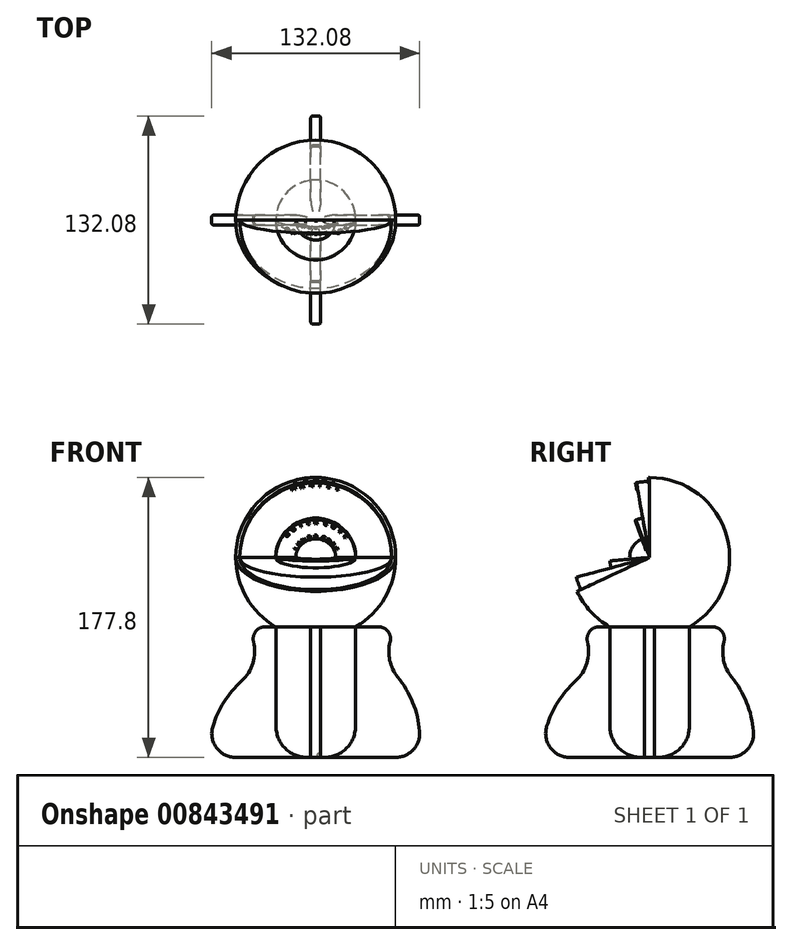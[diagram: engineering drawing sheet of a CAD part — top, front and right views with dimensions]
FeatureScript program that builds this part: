
annotation { "Feature Type Name" : "Feature", "Feature Type Description" : "" }
export const myFeature = defineFeature(function(context is Context, id is Id, definition is map)
    precondition{}
    {
        {
            var Q0;
            Q0=qCreatedBy(makeId("Front.planeOp"),FACE);
            var sketch = newSketch(context, id + "F0", { "sketchPlane" : qUnion([Q0])});
            skCircle(sketch, "E0", {"center": v(0, 0) * mm, "radius": 50.8 * mm});
            skLineSegment(sketch, "E1", {"start": v(-50.8, 0) * mm, "end": v(50.8, 0) * mm});
            skSolve(sketch);
        }
        {
            var Q0;
            {var subQ0=sQuery(id+"F0.wireOp",EDGE,"E1");Q0=makeQuery(id+"F0.imprint","IMPRINT",FACE,{"disambiguationData":[TD([[makeQuery(id+"F0.imprint","IMPRINT",EDGE,{"derivedFrom":subQ0}),1.0]])]});}
            var Q1;
            Q1=sQuery(id+"F0.wireOp",EDGE,"E1");
            revolve(context, id + "F1", {"surfaceOperationType" : NewSurfaceOperationType.NEW, "entities" : qUnion([Q0]), "axis" : qUnion([Q1]), "revolveType" : RevolveType.TWO_DIRECTIONS, "angle" : 0 * degree, "angleBack" : 115 * degree});
        }
        {
            var Q0;
            Q0=qCreatedBy(makeId("Front.planeOp"),FACE);
            var sketch = newSketch(context, id + "F2", { "sketchPlane" : qUnion([Q0])});
            skCircle(sketch, "E2", {"center": v(0, 0) * mm, "radius": 12.7 * mm});
            skLineSegment(sketch, "E3", {"start": v(-12.7, 0) * mm, "end": v(12.7, 0) * mm});
            skSolve(sketch);
        }
        {
            var Q0;
            {var subQ0=sQuery(id+"F2.wireOp",EDGE,"E3");Q0=makeQuery(id+"F2.imprint","IMPRINT",FACE,{"disambiguationData":[TD([[makeQuery(id+"F2.imprint","IMPRINT",EDGE,{"derivedFrom":subQ0}),1.0]])]});}
            var Q1;
            Q1=sQuery(id+"F2.wireOp",EDGE,"E3");
            revolve(context, id + "F3", {"operationType" : NewBodyOperationType.ADD, "surfaceOperationType" : NewSurfaceOperationType.NEW, "entities" : qUnion([Q0]), "axis" : qUnion([Q1]), "revolveType" : RevolveType.FULL});
        }
        {
            var Q0;
            Q0=qCreatedBy(makeId("Top.planeOp"),FACE);
            var sketch = newSketch(context, id + "F4", { "sketchPlane" : qUnion([Q0])});
            skCircle(sketch, "E4", {"center": v(0, 0) * mm, "radius": 25.4 * mm});
            skSolve(sketch);
        }
        {
            var Q0;
            Q0 = qSketchRegion(id + "F4", true);
            extrude(context, id + "F5", {"entities" : qUnion([Q0]), "operationType" : NewBodyOperationType.ADD, "oppositeDirection" : true, "depth" : 127 * mm, "offsetDistance" : 25.4 * mm, "hasSecondDirection" : true, "secondDirectionOppositeDirection" : true, "secondDirectionDepth" : 25.4 * mm});
        }
        {
            var Q0;
            Q0=makeQuery(id+"F5.opExtrude","CAP_EDGE",EDGE,{"disambiguationData":[OSD([sQuery(id+"F4.wireOp",EDGE,"E4")])],"isStart":false});
            fillet(context, id + "F6", {"entities" : qUnion([Q0]), "radius" : 19.62 * mm, "tangentPropagation" : true, "allowEdgeOverflow" : false});
        }
        {
            var Q0;
            Q0=qCreatedBy(makeId("Front.planeOp"),FACE);
            var sketch = newSketch(context, id + "F7", { "sketchPlane" : qUnion([Q0])});
            skCircle(sketch, "E5", {"center": v(0, 0) * mm, "radius": 48.26 * mm});
            skLineSegment(sketch, "E6", {"start": v(48.26, 0) * mm, "end": v(-48.26, 0) * mm});
            skSolve(sketch);
        }
        {
            var Q0;
            {var subQ0=sQuery(id+"F7.wireOp",EDGE,"E6");Q0=makeQuery(id+"F7.imprint","IMPRINT",FACE,{"disambiguationData":[TD([[makeQuery(id+"F7.imprint","IMPRINT",EDGE,{"derivedFrom":subQ0}),-1.0]])]});}
            var Q1;
            Q1=sQuery(id+"F0.wireOp",EDGE,"E1");
            revolve(context, id + "F8", {"operationType" : NewBodyOperationType.ADD, "surfaceOperationType" : NewSurfaceOperationType.NEW, "entities" : qUnion([Q0]), "axis" : qUnion([Q1]), "revolveType" : RevolveType.TWO_DIRECTIONS, "angle" : 10 * degree, "angleBack" : 105 * degree});
        }
        {
            var Q0;
            Q0=makeQuery(id+"F1.opRevolve","CAP_FACE",FACE,{"disambiguationData":[OSD([sQuery(id+"F0.wireOp",EDGE,"E0"),sQuery(id+"F0.wireOp",EDGE,"swF0dbNs-R56u-YkOw-oBFT-byD3DWGNXlO7")])],"isStart":false});
            var sketch = newSketch(context, id + "F9", { "sketchPlane" : qUnion([Q0])});
            skText(sketch, "E7", { "text": "C", "fontName": "OpenSans-Regular.ttf"});
            skText(sketch, "E8", { "text": "R", "fontName": "OpenSans-Regular.ttf"});
            skText(sketch, "E9", { "text": "U", "fontName": "OpenSans-Regular.ttf"});
            skText(sketch, "E10", { "text": "S", "fontName": "OpenSans-Regular.ttf"});
            skText(sketch, "E11", { "text": "T", "fontName": "OpenSans-Regular.ttf"});
            const initialGuessF9  = {"E7": [-0.01336, 0.04637, 0.96738, 0.25334, 0.00254], "E8": [-0.0076, 0.04766, 0.99104, 0.13356, 0.00254], "E9": [-0.0012, 0.04824, 0.99993, 0.01179, 0.00254], "E10": [0.00432, 0.04807, 0.99391, -0.11016, 0.00254], "E11": [0.01007, 0.0472, 0.97308, -0.23047, 0.00254]};
            skSetInitialGuess(sketch, initialGuessF9);
            skSolve(sketch);
        }
        {
            var Q0;
            Q0 = qSketchRegion(id + "F9", true);
            extrude(context, id + "F10", {"entities" : qUnion([Q0]), "operationType" : NewBodyOperationType.ADD, "depth" : 0.64 * mm, "offsetDistance" : 25.4 * mm});
        }
        {
            var Q0;
            Q0=makeQuery(id+"F8.opRevolve","CAP_FACE",FACE,{"disambiguationData":[OSD([sQuery(id+"F7.wireOp",EDGE,"E5"),sQuery(id+"F7.wireOp",EDGE,"E6")])],"isStart":false});
            var sketch = newSketch(context, id + "F11", { "sketchPlane" : qUnion([Q0])});
            skCircle(sketch, "E12", {"center": v(0, 0) * mm, "radius": 25.4 * mm});
            skPoint(sketch, "E13.startSnap0", {"position": v(0, 12.7) * mm});
            skLineSegment(sketch, "E14", {"start": v(-25.4, 0) * mm, "end": v(25.4, 0) * mm});
            skSolve(sketch);
        }
        {
            var Q0;
            {var subQ2=sQuery(id+"F7.wireOp",EDGE,"E6");var subQ6=makeQuery(id+"F8.boolean.opBoolean","INTERSECT",EDGE,{"derivedFrom":[makeQuery(id+"F3.opRevolve","SWEPT_FACE",FACE,{"disambiguationData":[OSD([sQuery(id+"F2.wireOp",EDGE,"E2")])]}),makeQuery(id+"F8.opRevolve","CAP_FACE",FACE,{"disambiguationData":[OSD([sQuery(id+"F7.wireOp",EDGE,"E5"),subQ2])],"isStart":false})]});Q0=makeQuery(id+"F11.imprint","IMPRINT",FACE,{"disambiguationData":[TD([[makeQuery(id+"F11.imprint","IMPRINT",EDGE,{"derivedFrom":subQ6}),-1.0]])]});}
            var Q1;
            Q1=sQuery(id+"F11.wireOp",EDGE,"E14");
            revolve(context, id + "F12", {"operationType" : NewBodyOperationType.ADD, "surfaceOperationType" : NewSurfaceOperationType.NEW, "entities" : qUnion([Q0]), "axis" : qUnion([Q1]), "revolveType" : RevolveType.TWO_DIRECTIONS, "angle" : 10 * degree, "angleBack" : 85 * degree});
        }
        {
            var Q0;
            {var subQ7=makeQuery(id+"F8.opRevolve","CAP_EDGE",EDGE,{"disambiguationData":[OSD([sQuery(id+"F7.wireOp",EDGE,"E5")])],"isStart":false});Q0=makeQuery(id+"F11.imprint","IMPRINT",FACE,{"disambiguationData":[TD([[makeQuery(id+"F11.imprint","IMPRINT",EDGE,{"derivedFrom":subQ7}),1.0]])]});}
            var sketch = newSketch(context, id + "F13", { "sketchPlane" : qUnion([Q0])});
            skCircle(sketch, "E15", {"center": v(0, 0) * mm, "radius": 45.72 * mm, "construction": true});
            skText(sketch, "E16", { "text": "M", "fontName": "OpenSans-Regular.ttf"});
            skText(sketch, "E17", { "text": "A", "fontName": "OpenSans-Regular.ttf"});
            skText(sketch, "E18", { "text": "N", "fontName": "OpenSans-Regular.ttf"});
            skText(sketch, "E19", { "text": "T", "fontName": "OpenSans-Regular.ttf"});
            skText(sketch, "E20", { "text": "L", "fontName": "OpenSans-Regular.ttf"});
            skText(sketch, "E21", { "text": "E", "fontName": "OpenSans-Regular.ttf"});
            skLineSegment(sketch, "E22", {"start": v(0, 45.72) * mm, "end": v(0, 48.26) * mm, "construction": true});
            const initialGuessF13  = {"E16": [-0.0153, 0.04309, 0.9531, 0.30266, 0.00254], "E17": [-0.00963, 0.0447, 0.98288, 0.18425, 0.00254], "E18": [-0.00415, 0.04553, 0.998, 0.0631, 0.00254], "E19": [0.00162, 0.0457, 0.99826, -0.059, 0.00254], "E20": [0.00726, 0.04514, 0.98363, -0.18022, 0.00254], "E21": [0.01271, 0.04392, 0.95433, -0.29875, 0.00254]};
            skSetInitialGuess(sketch, initialGuessF13);
            skSolve(sketch);
        }
        {
            var Q0;
            Q0 = qSketchRegion(id + "F13", true);
            extrude(context, id + "F14", {"entities" : qUnion([Q0]), "operationType" : NewBodyOperationType.ADD, "depth" : 0.64 * mm, "offsetDistance" : 25.4 * mm});
        }
        {
            var Q0;
            Q0=makeQuery(id+"F12.opRevolve","CAP_FACE",FACE,{"disambiguationData":[OSD([sQuery(id+"F2.wireOp",EDGE,"E2"),sQuery(id+"F7.wireOp",EDGE,"E5"),sQuery(id+"F7.wireOp",EDGE,"E6"),sQuery(id+"F11.wireOp",EDGE,"E12"),sQuery(id+"F11.wireOp",EDGE,"E14")])],"isStart":false});
            var sketch = newSketch(context, id + "F15", { "sketchPlane" : qUnion([Q0])});
            skCircle(sketch, "E23", {"center": v(0, 0) * mm, "radius": 22.86 * mm, "construction": true});
            skText(sketch, "E24", { "text": "O\n", "fontName": "OpenSans-Regular.ttf"});
            skText(sketch, "E25", { "text": "U", "fontName": "OpenSans-Regular.ttf"});
            skText(sketch, "E26", { "text": "T", "fontName": "OpenSans-Regular.ttf"});
            skText(sketch, "E27", { "text": "E", "fontName": "OpenSans-Regular.ttf"});
            skText(sketch, "E28", { "text": "R", "fontName": "OpenSans-Regular.ttf"});
            skText(sketch, "E29", { "text": "C", "fontName": "OpenSans-Regular.ttf"});
            skText(sketch, "E30", { "text": "O", "fontName": "OpenSans-Regular.ttf"});
            skText(sketch, "E31", { "text": "R", "fontName": "OpenSans-Regular.ttf"});
            skText(sketch, "E32", { "text": "E", "fontName": "OpenSans-Regular.ttf"});
            const initialGuessF15  = {"E24": [-0.01827, 0.01373, 0.64808, 0.76157, 0.00254], "E25": [-0.01462, 0.01757, 0.78574, 0.61856, 0.00254], "E26": [-0.01013, 0.0205, 0.91622, 0.40069, 0.00254], "E27": [-0.00562, 0.02216, 0.98946, 0.1448, 0.00255], "E28": [-0.00112, 0.02283, 0.99973, 0.02314, 0.00254], "E29": [0.00504, 0.0223, 0.9627, -0.27055, 0.00254], "E30": [0.00967, 0.02071, 0.87894, -0.47693, 0.00254], "E31": [0.01418, 0.01793, 0.75157, -0.65966, 0.00254], "E32": [0.01766, 0.01451, 0.60074, -0.79944, 0.00254]};
            skSetInitialGuess(sketch, initialGuessF15);
            skSolve(sketch);
        }
        {
            var Q0;
            Q0 = qSketchRegion(id + "F15", true);
            extrude(context, id + "F16", {"entities" : qUnion([Q0]), "operationType" : NewBodyOperationType.ADD, "depth" : 0.64 * mm, "offsetDistance" : 25.4 * mm});
        }
        {
            var Q0;
            Q0=qCreatedBy(makeId("Front.planeOp"),FACE);
            var sketch = newSketch(context, id + "F17", { "sketchPlane" : qUnion([Q0])});
            skLineSegment(sketch, "E33.left", {"start": v(0, -44) * mm, "end": v(52.06, -44) * mm});
            skLineSegment(sketch, "E33.right", {"start": v(0, -127) * mm, "end": v(50.8, -127) * mm});
            skArc(sketch, "E34", {"start": v(50.8, -127) * mm, "mid": v(62.03, -122.06) * mm, "end": v(65.98, -110.44) * mm});
            skArc(sketch, "E35", {"start": v(65.98, -110.44) * mm, "mid": v(61.6, -92.16) * mm, "end": v(52.06, -75.97) * mm});
            skArc(sketch, "E36", {"start": v(52.06, -75.97) * mm, "mid": v(46.4, -59.98) * mm, "end": v(52.06, -44) * mm});
            skLineSegment(sketch, "E37.MirrorCS", {"start": v(0, -44) * mm, "end": v(-44.13, -44) * mm});
            skArc(sketch, "E38.MirrorCS", {"start": v(-47.13, -78.48) * mm, "mid": v(-38.85, -61.83) * mm, "end": v(-44.13, -44) * mm});
            skArc(sketch, "E39.MirrorCS", {"start": v(-65.4, -107.39) * mm, "mid": v(-58.25, -91.68) * mm, "end": v(-47.13, -78.48) * mm});
            skArc(sketch, "E40.MirrorCS", {"start": v(-50.8, -127) * mm, "mid": v(-63.02, -120.86) * mm, "end": v(-65.4, -107.39) * mm});
            skLineSegment(sketch, "E41.MirrorCS", {"start": v(0, -127) * mm, "end": v(0, 0) * mm});
            skLineSegment(sketch, "E42.MirrorCS", {"start": v(0, -127) * mm, "end": v(-50.8, -127) * mm});
            skSolve(sketch);
        }
        {
            var Q0;
            Q0 = qSketchRegion(id + "F17", true);
            extrude(context, id + "F18", {"entities" : qUnion([Q0]), "operationType" : NewBodyOperationType.ADD, "depth" : 6.35 * mm, "offsetDistance" : 25.4 * mm, "symmetric" : true});
        }
        {
            var Q0;
            Q0=qCreatedBy(makeId("Right.planeOp"),FACE);
            var sketch = newSketch(context, id + "F19", { "sketchPlane" : qUnion([Q0])});
            skLineSegment(sketch, "E43.left", {"start": v(0, -44) * mm, "end": v(52.06, -44) * mm});
            skLineSegment(sketch, "E43.right", {"start": v(0, -127) * mm, "end": v(50.8, -127) * mm});
            skArc(sketch, "E44", {"start": v(50.8, -127) * mm, "mid": v(62.03, -122.06) * mm, "end": v(65.98, -110.44) * mm});
            skArc(sketch, "E45", {"start": v(65.98, -110.44) * mm, "mid": v(61.6, -92.16) * mm, "end": v(52.06, -75.97) * mm});
            skArc(sketch, "E46", {"start": v(52.06, -75.97) * mm, "mid": v(46.4, -59.98) * mm, "end": v(52.06, -44) * mm});
            skLineSegment(sketch, "E47.MirrorCS", {"start": v(0, -44) * mm, "end": v(-44.13, -44) * mm});
            skArc(sketch, "E48.MirrorCS", {"start": v(-47.13, -78.48) * mm, "mid": v(-38.85, -61.83) * mm, "end": v(-44.13, -44) * mm});
            skArc(sketch, "E49.MirrorCS", {"start": v(-65.4, -107.39) * mm, "mid": v(-58.25, -91.68) * mm, "end": v(-47.13, -78.48) * mm});
            skArc(sketch, "E50.MirrorCS", {"start": v(-50.8, -127) * mm, "mid": v(-63.02, -120.86) * mm, "end": v(-65.4, -107.39) * mm});
            skLineSegment(sketch, "E51.MirrorCS", {"start": v(0, -127) * mm, "end": v(0, 0) * mm});
            skLineSegment(sketch, "E52.MirrorCS", {"start": v(0, -127) * mm, "end": v(-50.8, -127) * mm});
            skSolve(sketch);
        }
        {
            var Q0;
            Q0 = qSketchRegion(id + "F19", true);
            extrude(context, id + "F20", {"entities" : qUnion([Q0]), "operationType" : NewBodyOperationType.ADD, "depth" : 6.35 * mm, "offsetDistance" : 25.4 * mm, "symmetric" : true});
        }
        {
            var Q0;
            Q0=makeQuery(id+"F18.opExtrude","SWEPT_EDGE",EDGE,{"disambiguationData":[OSD([sQuery(id+"F17.wireOp",EDGE,"E37.MirrorCS"),sQuery(id+"F17.wireOp",EDGE,"E38.MirrorCS")])]});
            var Q1;
            Q1=makeQuery(id+"F18.opExtrude","SWEPT_EDGE",EDGE,{"disambiguationData":[OSD([sQuery(id+"F17.wireOp",EDGE,"E33.left"),sQuery(id+"F17.wireOp",EDGE,"E36")])]});
            var Q2;
            Q2=makeQuery(id+"F20.opExtrude","SWEPT_EDGE",EDGE,{"disambiguationData":[OSD([sQuery(id+"F19.wireOp",EDGE,"E47.MirrorCS"),sQuery(id+"F19.wireOp",EDGE,"E48.MirrorCS")])]});
            var Q3;
            Q3=makeQuery(id+"F20.opExtrude","SWEPT_EDGE",EDGE,{"disambiguationData":[OSD([sQuery(id+"F19.wireOp",EDGE,"E43.left"),sQuery(id+"F19.wireOp",EDGE,"E46")])]});
            fillet(context, id + "F21", {"entities" : qUnion([Q0, Q1, Q2, Q3]), "radius" : 7.62 * mm, "tangentPropagation" : true, "allowEdgeOverflow" : false});
        }
        {
            var Q0;
            Q0=makeQuery(id+"F18.opExtrude","CAP_EDGE",EDGE,{"disambiguationData":[OSD([sQuery(id+"F17.wireOp",EDGE,"E38.MirrorCS")])],"isStart":false});
            var Q1;
            Q1=makeQuery(id+"F18.opExtrude","CAP_EDGE",EDGE,{"disambiguationData":[OSD([sQuery(id+"F17.wireOp",EDGE,"E38.MirrorCS")])],"isStart":true});
            var Q2;
            Q2=makeQuery(id+"F18.opExtrude","CAP_EDGE",EDGE,{"disambiguationData":[OSD([sQuery(id+"F17.wireOp",EDGE,"E36")])],"isStart":false});
            var Q3;
            Q3=makeQuery(id+"F18.opExtrude","CAP_EDGE",EDGE,{"disambiguationData":[OSD([sQuery(id+"F17.wireOp",EDGE,"E36")])],"isStart":true});
            var Q4;
            Q4=makeQuery(id+"F20.opExtrude","CAP_EDGE",EDGE,{"disambiguationData":[OSD([sQuery(id+"F19.wireOp",EDGE,"E48.MirrorCS")])],"isStart":true});
            var Q5;
            Q5=makeQuery(id+"F20.opExtrude","CAP_EDGE",EDGE,{"disambiguationData":[OSD([sQuery(id+"F19.wireOp",EDGE,"E46")])],"isStart":false});
            var Q6;
            Q6=makeQuery(id+"F20.opExtrude","CAP_EDGE",EDGE,{"disambiguationData":[OSD([sQuery(id+"F19.wireOp",EDGE,"E46")])],"isStart":true});
            var Q7;
            Q7=makeQuery(id+"F20.opExtrude","CAP_EDGE",EDGE,{"disambiguationData":[OSD([sQuery(id+"F19.wireOp",EDGE,"E48.MirrorCS")])],"isStart":false});
            fillet(context, id + "F22", {"entities" : qUnion([Q0, Q1, Q2, Q3, Q4, Q5, Q6, Q7]), "radius" : 1.23 * mm, "tangentPropagation" : true, "allowEdgeOverflow" : false});
        }
        {
            var Q0;
            {var subQ2=sQuery(id+"F11.wireOp",EDGE,"E14");var subQ3=sQuery(id+"F11.wireOp",EDGE,"E12");var subQ4=sQuery(id+"F7.wireOp",EDGE,"E6");var subQ5=sQuery(id+"F7.wireOp",EDGE,"E5");var subQ6=sQuery(id+"F2.wireOp",EDGE,"E2");Q0=makeQuery(id+"F16.boolean.opBoolean","SPLIT",FACE,{"disambiguationData":[TD([makeQuery(id+"F3.opRevolve","SWEPT_FACE",FACE,{"disambiguationData":[OSD([subQ6])]})])],"derivedFrom":makeQuery(id+"F12.opRevolve","CAP_FACE",FACE,{"disambiguationData":[OSD([subQ6,subQ5,subQ4,subQ3,subQ2])],"isStart":false})});}
            var sketch = newSketch(context, id + "F23", { "sketchPlane" : qUnion([Q0])});
            skCircle(sketch, "E53", {"center": v(0, 0) * mm, "radius": 15.24 * mm, "construction": true});
            skText(sketch, "E54", { "text": "I", "fontName": "OpenSans-Regular.ttf"});
            skText(sketch, "E55", { "text": "N", "fontName": "OpenSans-Regular.ttf"});
            skText(sketch, "E56", { "text": "N", "fontName": "OpenSans-Regular.ttf"});
            skText(sketch, "E57", { "text": "E", "fontName": "OpenSans-Regular.ttf"});
            skText(sketch, "E58", { "text": "R", "fontName": "OpenSans-Regular.ttf"});
            skText(sketch, "E59", { "text": "C", "fontName": "OpenSans-Regular.ttf"});
            skText(sketch, "E60", { "text": "O", "fontName": "OpenSans-Regular.ttf"});
            skText(sketch, "E61", { "text": "R", "fontName": "OpenSans-Regular.ttf"});
            skText(sketch, "E62", { "text": "E", "fontName": "OpenSans-Regular.ttf"});
            const initialGuessF23  = {"E54": [-0.01169, 0.00497, 0.42262, 0.9063, 0.00254], "E55": [-0.01037, 0.00733, 0.65606, 0.7547, 0.00255], "E56": [-0.00795, 0.0099, 0.83867, 0.54464, 0.00255], "E57": [-0.00444, 0.0119, 0.96126, 0.27564, 0.00255], "E58": [-0.00115, 0.0127, 1, 0, 0.0025], "E59": [0.00322, 0.01229, 0.9397, -0.34202, 0.00255], "E60": [0.0061, 0.01114, 0.81915, -0.57358, 0.00255], "E61": [0.00893, 0.00903, 0.64279, -0.76604, 0.00255], "E62": [0.01106, 0.00625, 0.42262, -0.9063, 0.00255]};
            skSetInitialGuess(sketch, initialGuessF23);
            skSolve(sketch);
        }
        {
            var Q0;
            Q0 = qSketchRegion(id + "F23", true);
            extrude(context, id + "F24", {"entities" : qUnion([Q0]), "domain" : OperationDomain.MODEL, "operationType" : NewBodyOperationType.ADD, "flatOperationType" : FlatOperationType.REMOVE, "depth" : 0.65 * mm, "offsetDistance" : 25.4 * mm});
        }
    });
